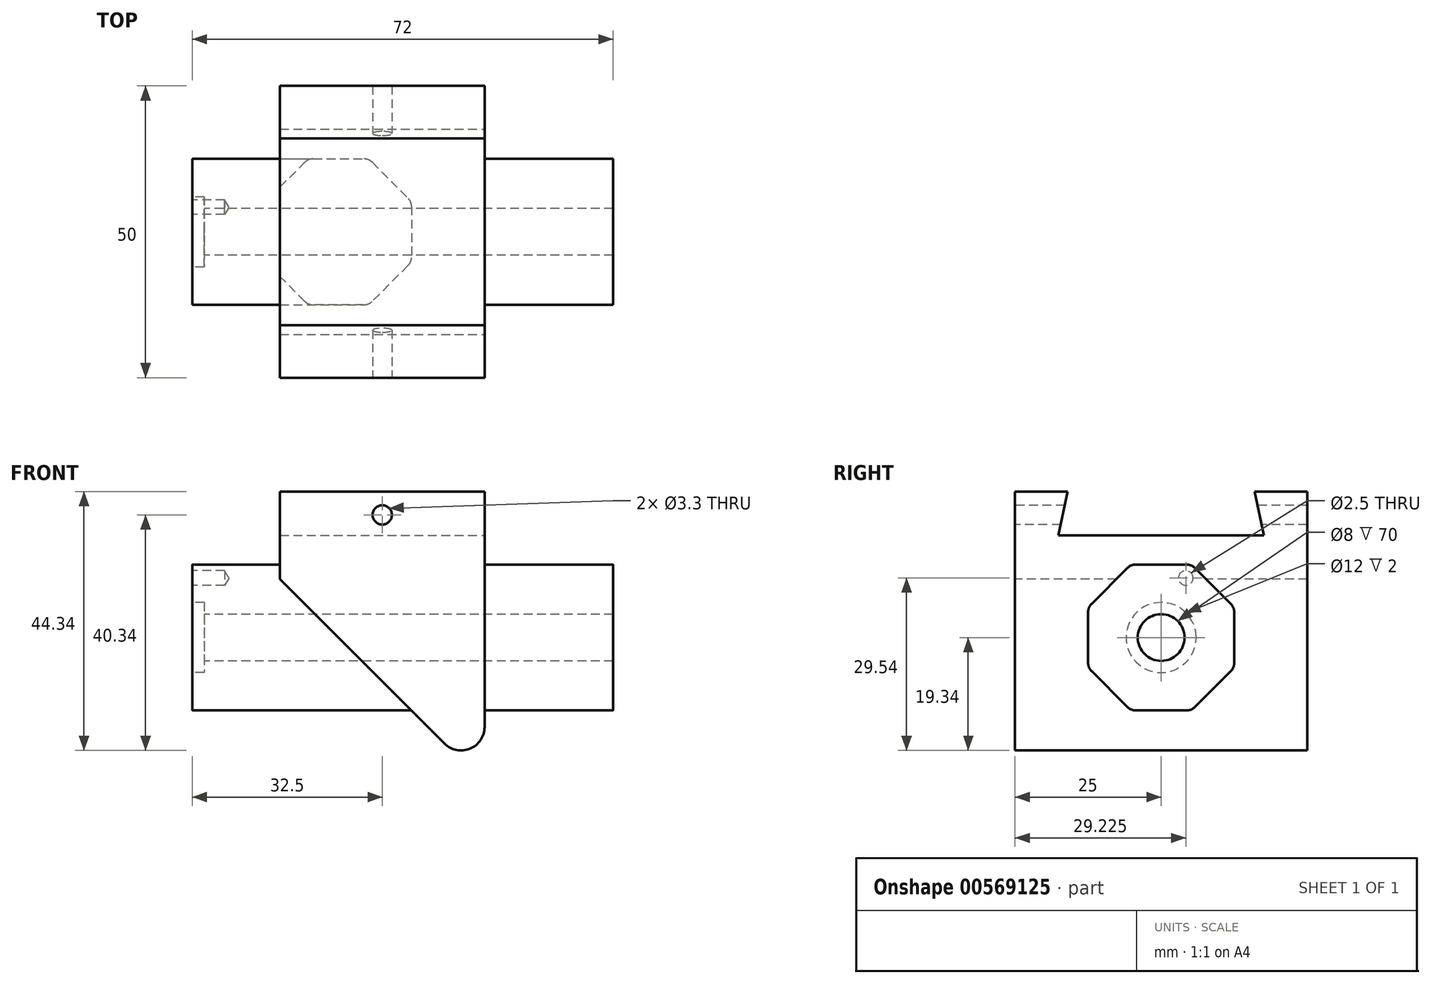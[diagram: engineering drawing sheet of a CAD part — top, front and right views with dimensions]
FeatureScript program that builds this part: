
annotation { "Feature Type Name" : "Feature", "Feature Type Description" : "" }
export const myFeature = defineFeature(function(context is Context, id is Id, definition is map)
    precondition{}
    {
        {
            var Q0;
            Q0=qCreatedBy(makeId("Front.planeOp"),FACE);
            var sketch = newSketch(context, id + "F0", { "sketchPlane" : qUnion([Q0])});
            skLineSegment(sketch, "E0.bottom", {"start": v(-17.5, 25) * mm, "end": v(17.5, 25) * mm});
            skLineSegment(sketch, "E0.top", {"start": v(-17.5, -25) * mm, "end": v(17.5, -25) * mm});
            skLineSegment(sketch, "E0.left", {"start": v(-17.5, 25) * mm, "end": v(-17.5, -25) * mm});
            skLineSegment(sketch, "E0.right", {"start": v(17.5, 25) * mm, "end": v(17.5, -25) * mm});
            skSolve(sketch);
        }
        {
            var Q0;
            Q0 = qSketchRegion(id + "F0", true);
            extrude(context, id + "F1", {"entities" : qUnion([Q0]), "depth" : 50 * mm, "offsetDistance" : 25 * mm});
        }
        {
            var Q0;
            Q0=makeQuery(id+"F1.opExtrude","CAP_FACE",FACE,{"disambiguationData":[OSD([sQuery(id+"F0.wireOp",EDGE,"E0.bottom"),sQuery(id+"F0.wireOp",EDGE,"E0.top"),sQuery(id+"F0.wireOp",EDGE,"E0.left"),sQuery(id+"F0.wireOp",EDGE,"E0.right")])],"isStart":false});
            var sketch = newSketch(context, id + "F2", { "sketchPlane" : qUnion([Q0])});
            skPoint(sketch, "E1", {"position": v(0, 21) * mm});
            skSolve(sketch);
        }
        {
            var Q0;
            Q0=sQuery(id+"F2.wireOp",VERTEX,"E1");
            var Q1;
            Q1=makeQuery(id+"F1.opExtrude","SWEPT_BODY",BODY,{"disambiguationData":[OSD([sQuery(id+"F0.wireOp",EDGE,"E0.bottom"),sQuery(id+"F0.wireOp",EDGE,"E0.top"),sQuery(id+"F0.wireOp",EDGE,"E0.left"),sQuery(id+"F0.wireOp",EDGE,"E0.right")])]});
            hole(context, id + "F3", {"style" : HoleStyle.SIMPLE, "endStyle" : HoleEndStyle.THROUGH, "standardTappedOrClearance" : lookupTablePath({ "standard" : "ISO", "fit" : "Normal", "engagement" : "75%", "pitch" : "0.7 mm", "size" : "M4", "type" : "Tapped" }), "standardBlindInLast" : lookupTablePath({ "fit" : "Standard", "standard" : "ISO", "engagement" : "75%", "pitch" : "0.7 mm", "size" : "M4", "type" : "Tapped" }), "holeDiameter" : 3.3 * mm, "showTappedDepth" : true, "isTappedThrough" : true, "tappedDepth" : 12 * mm, "tapClearance" : 3, "locations" : qUnion([Q0]), "scope" : qUnion([Q1]), "majorDiameter" : 4 * mm});
        }
        {
            var Q0;
            Q0=makeQuery(id+"F1.opExtrude","SWEPT_FACE",FACE,{"disambiguationData":[OSD([sQuery(id+"F0.wireOp",EDGE,"E0.right")])]});
            var sketch = newSketch(context, id + "F4", { "sketchPlane" : qUnion([Q0])});
            skLineSegment(sketch, "E2", {"start": v(-41, 25) * mm, "end": v(-42.6, 17.5) * mm});
            skLineSegment(sketch, "E3", {"start": v(-42.6, 17.5) * mm, "end": v(-7.4, 17.5) * mm});
            skLineSegment(sketch, "E4", {"start": v(-7.4, 17.5) * mm, "end": v(-9, 25) * mm});
            skLineSegment(sketch, "E5", {"start": v(-9, 25) * mm, "end": v(-41, 25) * mm});
            skSolve(sketch);
        }
        {
            var Q0;
            Q0=makeQuery(id+"F4.imprint","IMPRINT",FACE,{"disambiguationData":[TD([[makeQuery(id+"F4.imprint","IMPRINT",EDGE,{"derivedFrom":sQuery(id+"F4.wireOp",EDGE,"E2")}),1.0]])]});
            extrude(context, id + "F5", {"entities" : qUnion([Q0]), "operationType" : NewBodyOperationType.REMOVE, "endBound" : BoundingType.THROUGH_ALL, "oppositeDirection" : true, "depth" : 25 * mm, "offsetDistance" : 25 * mm});
        }
        {
            var Q0;
            Q0=makeQuery(id+"F1.opExtrude","SWEPT_FACE",FACE,{"disambiguationData":[OSD([sQuery(id+"F0.wireOp",EDGE,"E0.right")])]});
            var sketch = newSketch(context, id + "F6", { "sketchPlane" : qUnion([Q0])});
            skPoint(sketch, "E6", {"position": v(-25, 0) * mm});
            skCircle(sketch, "E7.cCircle", {"center": v(-25, 0) * mm, "radius": 12.5 * mm, "construction": true});
            skLineSegment(sketch, "E7.0", {"start": v(-19.82, -12.5) * mm, "end": v(-30.18, -12.5) * mm});
            skLineSegment(sketch, "E7.1", {"start": v(-30.18, -12.5) * mm, "end": v(-37.5, -5.18) * mm});
            skLineSegment(sketch, "E7.2", {"start": v(-37.5, -5.18) * mm, "end": v(-37.5, 5.18) * mm});
            skLineSegment(sketch, "E7.3", {"start": v(-37.5, 5.18) * mm, "end": v(-30.18, 12.5) * mm});
            skLineSegment(sketch, "E7.4", {"start": v(-30.18, 12.5) * mm, "end": v(-19.82, 12.5) * mm});
            skLineSegment(sketch, "E7.5", {"start": v(-19.82, 12.5) * mm, "end": v(-12.5, 5.18) * mm});
            skLineSegment(sketch, "E7.6", {"start": v(-12.5, 5.18) * mm, "end": v(-12.5, -5.18) * mm});
            skLineSegment(sketch, "E7.7", {"start": v(-12.5, -5.18) * mm, "end": v(-19.82, -12.5) * mm});
            skPoint(sketch, "E7.0.midPoint", {"position": v(-25, -12.5) * mm});
            skSolve(sketch);
        }
        {
            var Q0;
            Q0=makeQuery(id+"F6.imprint","IMPRINT",FACE,{"disambiguationData":[TD([[makeQuery(id+"F6.imprint","IMPRINT",EDGE,{"derivedFrom":sQuery(id+"F6.wireOp",EDGE,"E7.0")}),-1.0]])]});
            extrude(context, id + "F7", {"entities" : qUnion([Q0]), "operationType" : NewBodyOperationType.ADD, "depth" : 22 * mm, "offsetDistance" : 25 * mm});
        }
        {
            var Q0;
            Q0=makeQuery(id+"F1.opExtrude","CAP_FACE",FACE,{"disambiguationData":[OSD([sQuery(id+"F0.wireOp",EDGE,"E0.bottom"),sQuery(id+"F0.wireOp",EDGE,"E0.top"),sQuery(id+"F0.wireOp",EDGE,"E0.left"),sQuery(id+"F0.wireOp",EDGE,"E0.right")])],"isStart":true});
            var sketch = newSketch(context, id + "F8", { "sketchPlane" : qUnion([Q0])});
            skLineSegment(sketch, "E8", {"start": v(31.74, 24.24) * mm, "end": v(-17.5, -25) * mm});
            skLineSegment(sketch, "E9", {"start": v(-17.5, -25) * mm, "end": v(22.93, -42.56) * mm});
            skLineSegment(sketch, "E10", {"start": v(22.93, -42.56) * mm, "end": v(55.8, -0.9) * mm});
            skLineSegment(sketch, "E11", {"start": v(55.8, -0.9) * mm, "end": v(31.74, 24.24) * mm});
            skSolve(sketch);
        }
        {
            var Q0;
            Q0=makeQuery(id+"F8.imprint","IMPRINT",FACE,{"disambiguationData":[TD([[makeQuery(id+"F8.imprint","IMPRINT",EDGE,{"derivedFrom":sQuery(id+"F8.wireOp",EDGE,"E9")}),1.0]])]});
            var Q1;
            {var subQ1=makeQuery(id+"F1.opExtrude","CAP_EDGE",EDGE,{"disambiguationData":[OSD([sQuery(id+"F0.wireOp",EDGE,"E0.top")])],"isStart":true});Q1=makeQuery(id+"F8.imprint","IMPRINT",FACE,{"disambiguationData":[TD([[makeQuery(id+"F8.imprint","IMPRINT",EDGE,{"derivedFrom":subQ1}),-1.0]])]});}
            extrude(context, id + "F9", {"entities" : qUnion([Q0, Q1]), "operationType" : NewBodyOperationType.REMOVE, "endBound" : BoundingType.THROUGH_ALL, "oppositeDirection" : true, "depth" : 25 * mm, "offsetDistance" : 25 * mm});
        }
        {
            var Q0;
            {var subQ0=sQuery(id+"F0.wireOp",EDGE,"E0.right");var subQ1=sQuery(id+"F0.wireOp",EDGE,"E0.top");Q0=makeQuery(id+"F9.boolean.opBoolean","MERGE",EDGE,{"derivedFrom":[makeQuery(id+"F1.opExtrude","SWEPT_EDGE",EDGE,{"disambiguationData":[OSD([subQ1,subQ0])]}),makeQuery(id+"F9.opExtrude","SWEPT_EDGE",EDGE,{"disambiguationData":[OSD([subQ1,subQ0,sQuery(id+"F8.wireOp",EDGE,"E8"),sQuery(id+"F8.wireOp",EDGE,"E9")])]})]});}
            fillet(context, id + "F10", {"entities" : qUnion([Q0]), "radius" : 4 * mm, "tangentPropagation" : true, "allowEdgeOverflow" : false});
        }
        {
            var Q0;
            Q0=makeQuery(id+"F1.opExtrude","SWEPT_FACE",FACE,{"disambiguationData":[OSD([sQuery(id+"F0.wireOp",EDGE,"E0.right")])]});
            var sketch = newSketch(context, id + "F11", { "sketchPlane" : qUnion([Q0])});
            skLineSegment(sketch, "E12.0", {"start": v(-19.82, 12.5) * mm, "end": v(-12.5, 5.18) * mm});
            skLineSegment(sketch, "E13.0", {"start": v(-30.18, 12.5) * mm, "end": v(-19.82, 12.5) * mm});
            skLineSegment(sketch, "E14.0.0", {"start": v(-19.82, -12.5) * mm, "end": v(-12.5, -5.18) * mm});
            skLineSegment(sketch, "E14.0.1", {"start": v(-12.5, -5.18) * mm, "end": v(-12.5, 5.18) * mm});
            skLineSegment(sketch, "E14.0.2", {"start": v(-12.5, 5.18) * mm, "end": v(-19.82, 12.5) * mm});
            skLineSegment(sketch, "E14.0.3", {"start": v(-19.82, 12.5) * mm, "end": v(-30.18, 12.5) * mm});
            skLineSegment(sketch, "E14.0.4", {"start": v(-30.18, 12.5) * mm, "end": v(-37.5, 5.18) * mm});
            skLineSegment(sketch, "E14.0.5", {"start": v(-37.5, 5.18) * mm, "end": v(-37.5, -5.18) * mm});
            skLineSegment(sketch, "E14.0.6", {"start": v(-37.5, -5.18) * mm, "end": v(-30.18, -12.5) * mm});
            skLineSegment(sketch, "E14.0.7", {"start": v(-30.18, -12.5) * mm, "end": v(-19.82, -12.5) * mm});
            skSolve(sketch);
        }
        {
            var Q0;
            Q0=makeQuery(id+"F7.opExtrude","CAP_FACE",FACE,{"disambiguationData":[OSD([sQuery(id+"F6.wireOp",EDGE,"E7.0"),sQuery(id+"F6.wireOp",EDGE,"E7.1"),sQuery(id+"F6.wireOp",EDGE,"E7.2"),sQuery(id+"F6.wireOp",EDGE,"E7.3"),sQuery(id+"F6.wireOp",EDGE,"E7.4"),sQuery(id+"F6.wireOp",EDGE,"E7.5"),sQuery(id+"F6.wireOp",EDGE,"E7.6"),sQuery(id+"F6.wireOp",EDGE,"E7.7")])],"isStart":false});
            extrude(context, id + "F12", {"entities" : qUnion([Q0]), "operationType" : NewBodyOperationType.ADD, "oppositeDirection" : true, "depth" : 72 * mm, "offsetDistance" : 25 * mm});
        }
        {
            var Q0;
            Q0=makeQuery(id+"F12.opExtrude","CAP_FACE",FACE,{"disambiguationData":[OSD([sQuery(id+"F6.wireOp",EDGE,"E7.0"),sQuery(id+"F6.wireOp",EDGE,"E7.1"),sQuery(id+"F6.wireOp",EDGE,"E7.2"),sQuery(id+"F6.wireOp",EDGE,"E7.3"),sQuery(id+"F6.wireOp",EDGE,"E7.4"),sQuery(id+"F6.wireOp",EDGE,"E7.5"),sQuery(id+"F6.wireOp",EDGE,"E7.6"),sQuery(id+"F6.wireOp",EDGE,"E7.7")])],"isStart":false});
            var sketch = newSketch(context, id + "F13", { "sketchPlane" : qUnion([Q0])});
            skPoint(sketch, "E15", {"position": v(20.78, 10.2) * mm});
            skSolve(sketch);
        }
        {
            var Q0;
            Q0=sQuery(id+"F13.wireOp",VERTEX,"E15");
            var Q1;
            Q1=makeQuery(id+"F1.opExtrude","SWEPT_BODY",BODY,{"disambiguationData":[OSD([sQuery(id+"F0.wireOp",EDGE,"E0.bottom"),sQuery(id+"F0.wireOp",EDGE,"E0.top"),sQuery(id+"F0.wireOp",EDGE,"E0.left"),sQuery(id+"F0.wireOp",EDGE,"E0.right")])]});
            hole(context, id + "F14", {"style" : HoleStyle.SIMPLE, "endStyle" : HoleEndStyle.BLIND, "standardTappedOrClearance" : lookupTablePath({ "standard" : "ISO", "fit" : "Normal", "engagement" : "75%", "pitch" : "0.5 mm", "size" : "M3", "type" : "Tapped" }), "standardBlindInLast" : lookupTablePath({ "fit" : "Standard", "standard" : "ISO", "engagement" : "75%", "pitch" : "0.5 mm", "size" : "M3", "type" : "Tapped" }), "holeDiameter" : 2.5 * mm, "showTappedDepth" : true, "holeDepth" : 5.5 * mm, "tappedDepth" : 4 * mm, "tapClearance" : 3, "locations" : qUnion([Q0]), "scope" : qUnion([Q1]), "majorDiameter" : 3 * mm});
        }
        {
            var Q0;
            Q0=makeQuery(id+"F12.opExtrude","CAP_FACE",FACE,{"disambiguationData":[OSD([sQuery(id+"F6.wireOp",EDGE,"E7.0"),sQuery(id+"F6.wireOp",EDGE,"E7.1"),sQuery(id+"F6.wireOp",EDGE,"E7.2"),sQuery(id+"F6.wireOp",EDGE,"E7.3"),sQuery(id+"F6.wireOp",EDGE,"E7.4"),sQuery(id+"F6.wireOp",EDGE,"E7.5"),sQuery(id+"F6.wireOp",EDGE,"E7.6"),sQuery(id+"F6.wireOp",EDGE,"E7.7")])],"isStart":false});
            var sketch = newSketch(context, id + "F15", { "sketchPlane" : qUnion([Q0])});
            skPoint(sketch, "E16", {"position": v(25, 0) * mm});
            skSolve(sketch);
        }
        {
            var Q0;
            Q0=sQuery(id+"F15.wireOp",VERTEX,"E16");
            var Q1;
            Q1=makeQuery(id+"F1.opExtrude","SWEPT_BODY",BODY,{"disambiguationData":[OSD([sQuery(id+"F0.wireOp",EDGE,"E0.bottom"),sQuery(id+"F0.wireOp",EDGE,"E0.top"),sQuery(id+"F0.wireOp",EDGE,"E0.left"),sQuery(id+"F0.wireOp",EDGE,"E0.right")])]});
            hole(context, id + "F16", {"style" : HoleStyle.C_BORE, "endStyle" : HoleEndStyle.THROUGH, "holeDiameter" : 8 * mm, "cBoreDiameter" : 12 * mm, "cBoreDepth" : 2 * mm, "isTappedThrough" : true, "tappedDepth" : 12 * mm, "tapClearance" : 3, "startFromSketch" : true, "locations" : qUnion([Q0]), "scope" : qUnion([Q1])});
        }
        {
            var Q0;
            Q0=makeQuery(id+"F12.opExtrude","SWEPT_EDGE",EDGE,{"disambiguationData":[OSD([sQuery(id+"F6.wireOp",EDGE,"E7.3"),sQuery(id+"F6.wireOp",EDGE,"E7.4")])]});
            var Q1;
            Q1=makeQuery(id+"F12.opExtrude","SWEPT_EDGE",EDGE,{"disambiguationData":[OSD([sQuery(id+"F6.wireOp",EDGE,"E7.2"),sQuery(id+"F6.wireOp",EDGE,"E7.3")])]});
            var Q2;
            Q2=makeQuery(id+"F12.opExtrude","SWEPT_EDGE",EDGE,{"disambiguationData":[OSD([sQuery(id+"F6.wireOp",EDGE,"E7.1"),sQuery(id+"F6.wireOp",EDGE,"E7.2")])]});
            var Q3;
            Q3=makeQuery(id+"F12.opExtrude","SWEPT_EDGE",EDGE,{"disambiguationData":[OSD([sQuery(id+"F6.wireOp",EDGE,"E7.0"),sQuery(id+"F6.wireOp",EDGE,"E7.1")])]});
            var Q4;
            Q4=makeQuery(id+"F12.opExtrude","SWEPT_EDGE",EDGE,{"disambiguationData":[OSD([sQuery(id+"F6.wireOp",EDGE,"E7.0"),sQuery(id+"F6.wireOp",EDGE,"E7.7")])]});
            var Q5;
            Q5=makeQuery(id+"F12.opExtrude","SWEPT_EDGE",EDGE,{"disambiguationData":[OSD([sQuery(id+"F6.wireOp",EDGE,"E7.6"),sQuery(id+"F6.wireOp",EDGE,"E7.7")])]});
            var Q6;
            Q6=makeQuery(id+"F12.opExtrude","SWEPT_EDGE",EDGE,{"disambiguationData":[OSD([sQuery(id+"F6.wireOp",EDGE,"E7.4"),sQuery(id+"F6.wireOp",EDGE,"E7.5")])]});
            var Q7;
            Q7=makeQuery(id+"F12.opExtrude","SWEPT_EDGE",EDGE,{"disambiguationData":[OSD([sQuery(id+"F6.wireOp",EDGE,"E7.5"),sQuery(id+"F6.wireOp",EDGE,"E7.6")])]});
            var Q8;
            Q8=makeQuery(id+"F7.opExtrude","SWEPT_EDGE",EDGE,{"disambiguationData":[OSD([sQuery(id+"F6.wireOp",EDGE,"E7.5"),sQuery(id+"F6.wireOp",EDGE,"E7.6")])]});
            var Q9;
            Q9=makeQuery(id+"F7.opExtrude","SWEPT_EDGE",EDGE,{"disambiguationData":[OSD([sQuery(id+"F6.wireOp",EDGE,"E7.6"),sQuery(id+"F6.wireOp",EDGE,"E7.7")])]});
            var Q10;
            Q10=makeQuery(id+"F7.opExtrude","SWEPT_EDGE",EDGE,{"disambiguationData":[OSD([sQuery(id+"F6.wireOp",EDGE,"E7.0"),sQuery(id+"F6.wireOp",EDGE,"E7.7")])]});
            var Q11;
            Q11=makeQuery(id+"F7.opExtrude","SWEPT_EDGE",EDGE,{"disambiguationData":[OSD([sQuery(id+"F6.wireOp",EDGE,"E7.0"),sQuery(id+"F6.wireOp",EDGE,"E7.1")])]});
            var Q12;
            Q12=makeQuery(id+"F7.opExtrude","SWEPT_EDGE",EDGE,{"disambiguationData":[OSD([sQuery(id+"F6.wireOp",EDGE,"E7.1"),sQuery(id+"F6.wireOp",EDGE,"E7.2")])]});
            var Q13;
            Q13=makeQuery(id+"F7.opExtrude","SWEPT_EDGE",EDGE,{"disambiguationData":[OSD([sQuery(id+"F6.wireOp",EDGE,"E7.2"),sQuery(id+"F6.wireOp",EDGE,"E7.3")])]});
            var Q14;
            Q14=makeQuery(id+"F7.opExtrude","SWEPT_EDGE",EDGE,{"disambiguationData":[OSD([sQuery(id+"F6.wireOp",EDGE,"E7.3"),sQuery(id+"F6.wireOp",EDGE,"E7.4")])]});
            var Q15;
            Q15=makeQuery(id+"F7.opExtrude","SWEPT_EDGE",EDGE,{"disambiguationData":[OSD([sQuery(id+"F6.wireOp",EDGE,"E7.4"),sQuery(id+"F6.wireOp",EDGE,"E7.5")])]});
            fillet(context, id + "F17", {"entities" : qUnion([Q0, Q1, Q2, Q3, Q4, Q5, Q6, Q7, Q8, Q9, Q10, Q11, Q12, Q13, Q14, Q15]), "radius" : 2 * mm, "tangentPropagation" : true, "allowEdgeOverflow" : false});
        }
    });
